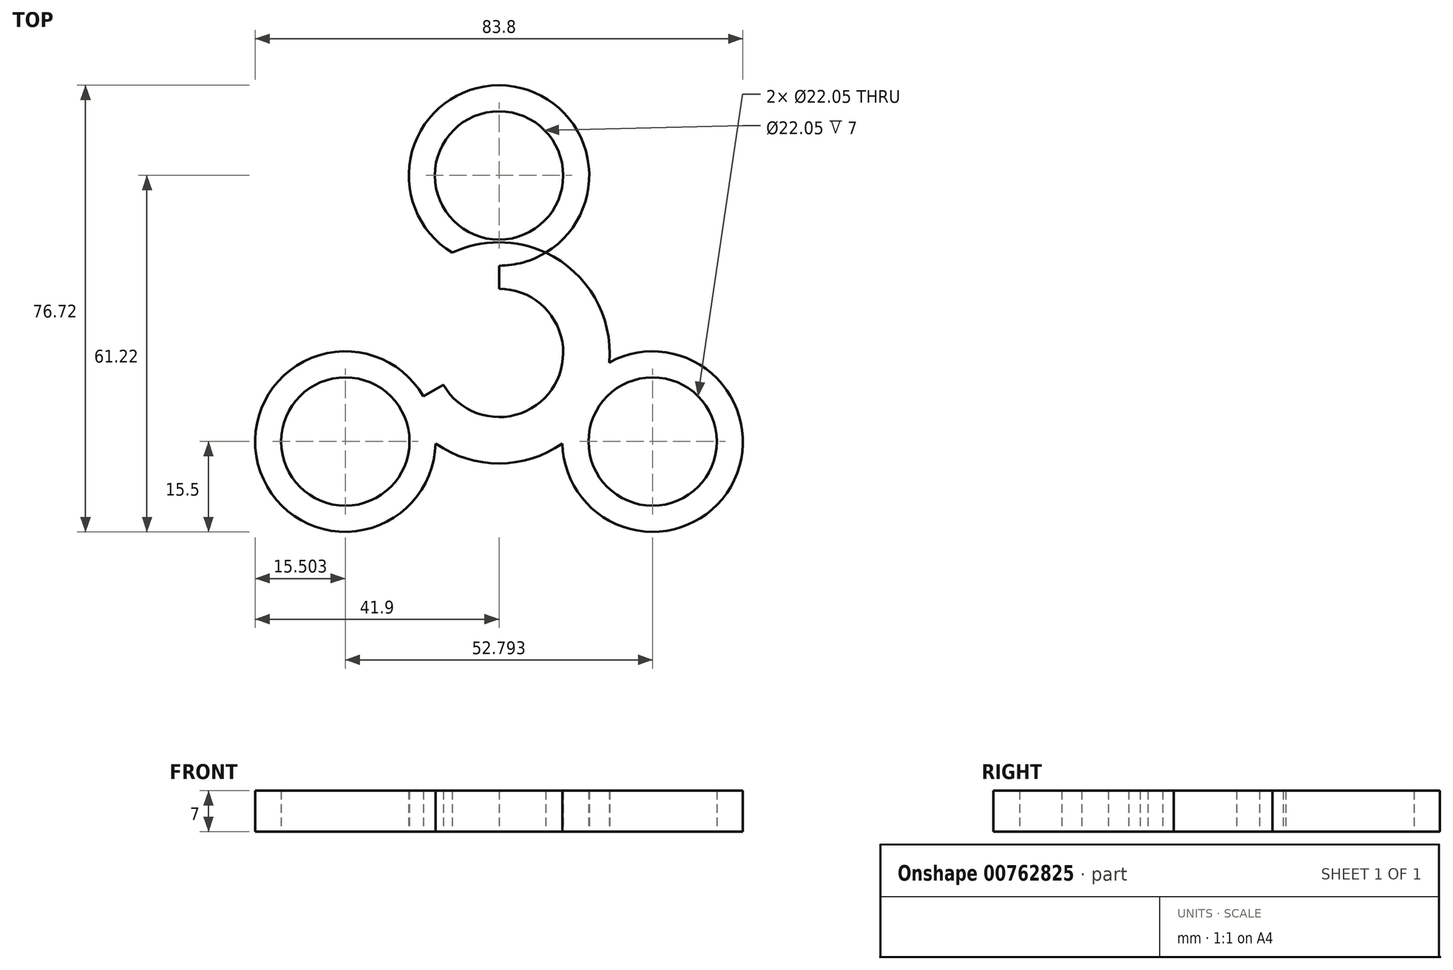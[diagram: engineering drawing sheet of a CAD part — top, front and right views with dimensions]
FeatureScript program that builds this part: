
annotation { "Feature Type Name" : "Feature", "Feature Type Description" : "" }
export const myFeature = defineFeature(function(context is Context, id is Id, definition is map)
    precondition{}
    {
        {
            var Q0;
            Q0=qCreatedBy(makeId("Top.planeOp"),FACE);
            var sketch = newSketch(context, id + "F0", { "sketchPlane" : qUnion([Q0])});
            skCircle(sketch, "E0", {"center": v(0, 0) * mm, "radius": 11.03 * mm});
            skLineSegment(sketch, "E1", {"start": v(0, 0) * mm, "end": v(0, 30.48) * mm});
            skLineSegment(sketch, "E2", {"start": v(0, 30.48) * mm, "end": v(0, 0) * mm});
            skLineSegment(sketch, "E3", {"start": v(0, 0) * mm, "end": v(26.4, -15.24) * mm});
            skLineSegment(sketch, "E4", {"start": v(0, 0) * mm, "end": v(-26.4, -15.24) * mm});
            skCircle(sketch, "E5", {"center": v(0, 30.48) * mm, "radius": 11.03 * mm});
            skCircle(sketch, "E6", {"center": v(26.4, -15.24) * mm, "radius": 11.03 * mm});
            skCircle(sketch, "E7", {"center": v(-26.4, -15.24) * mm, "radius": 11.03 * mm});
            skCircle(sketch, "E8", {"center": v(0, 30.48) * mm, "radius": 15.5 * mm});
            skCircle(sketch, "E9", {"center": v(26.4, -15.24) * mm, "radius": 15.5 * mm});
            skCircle(sketch, "E10", {"center": v(-26.4, -15.24) * mm, "radius": 15.5 * mm});
            skCircle(sketch, "E11", {"center": v(0, 0) * mm, "radius": 19 * mm});
            skLineSegment(sketch, "E12", {"start": v(18.98, 0.97) * mm, "end": v(8.47, 7.06) * mm});
            skSolve(sketch);
        }
        {
            var Q0;
            Q0=makeQuery(id+"F0.imprint","IMPRINT",FACE,{"disambiguationData":[TD([[makeQuery(id+"F0.imprint","IMPRINT",EDGE,{"derivedFrom":sQuery(id+"F0.wireOp",EDGE,"E5")}),-1.0]])]});
            var Q1;
            {var subQ0=sQuery(id+"F0.wireOp",EDGE,"E2");var subQ1=sQuery(id+"F0.wireOp",EDGE,"E0");var subQ2=makeQuery(id+"F0.imprint","INTERSECT",VERTEX,{"derivedFrom":[subQ1,subQ0]});Q1=makeQuery(id+"F0.imprint","IMPRINT",FACE,{"disambiguationData":[TD([[makeQuery(id+"F0.imprint","IMPRINT",EDGE,{"disambiguationData":[TD([[subQ2,-1.0]])],"derivedFrom":subQ1}),-1.0]])]});}
            var Q2;
            {var subQ5=sQuery(id+"F0.wireOp",EDGE,"E12");Q2=makeQuery(id+"F0.imprint","IMPRINT",FACE,{"disambiguationData":[TD([[makeQuery(id+"F0.imprint","IMPRINT",EDGE,{"derivedFrom":subQ5}),-1.0]])]});}
            var Q3;
            {var subQ0=sQuery(id+"F0.wireOp",EDGE,"E11");var subQ1=sQuery(id+"F0.wireOp",EDGE,"E2");var subQ2=makeQuery(id+"F0.imprint","INTERSECT",VERTEX,{"derivedFrom":[subQ1,subQ0]});Q3=makeQuery(id+"F0.imprint","IMPRINT",FACE,{"disambiguationData":[TD([[makeQuery(id+"F0.imprint","IMPRINT",EDGE,{"disambiguationData":[TD([[subQ2,-1.0]])],"derivedFrom":subQ1}),1.0]])]});}
            var Q4;
            {var subQ0=sQuery(id+"F0.wireOp",EDGE,"E11");var subQ1=sQuery(id+"F0.wireOp",EDGE,"E2");var subQ2=makeQuery(id+"F0.imprint","INTERSECT",VERTEX,{"derivedFrom":[subQ1,subQ0]});Q4=makeQuery(id+"F0.imprint","IMPRINT",FACE,{"disambiguationData":[TD([[makeQuery(id+"F0.imprint","IMPRINT",EDGE,{"disambiguationData":[TD([[subQ2,-1.0]])],"derivedFrom":subQ1}),-1.0]])]});}
            var Q5;
            Q5=makeQuery(id+"F0.imprint","IMPRINT",FACE,{"disambiguationData":[TD([[makeQuery(id+"F0.imprint","IMPRINT",EDGE,{"derivedFrom":sQuery(id+"F0.wireOp",EDGE,"E7")}),-1.0]])]});
            var Q6;
            {var subQ0=sQuery(id+"F0.wireOp",EDGE,"E11");var subQ1=sQuery(id+"F0.wireOp",EDGE,"E4");var subQ2=makeQuery(id+"F0.imprint","INTERSECT",VERTEX,{"derivedFrom":[subQ1,subQ0]});Q6=makeQuery(id+"F0.imprint","IMPRINT",FACE,{"disambiguationData":[TD([[makeQuery(id+"F0.imprint","IMPRINT",EDGE,{"disambiguationData":[TD([[subQ2,1.0]])],"derivedFrom":subQ1}),-1.0]])]});}
            var Q7;
            {var subQ0=sQuery(id+"F0.wireOp",EDGE,"E11");var subQ1=sQuery(id+"F0.wireOp",EDGE,"E4");var subQ2=makeQuery(id+"F0.imprint","INTERSECT",VERTEX,{"derivedFrom":[subQ1,subQ0]});Q7=makeQuery(id+"F0.imprint","IMPRINT",FACE,{"disambiguationData":[TD([[makeQuery(id+"F0.imprint","IMPRINT",EDGE,{"disambiguationData":[TD([[subQ2,1.0]])],"derivedFrom":subQ1}),1.0]])]});}
            var Q8;
            {var subQ7=sQuery(id+"F0.wireOp",EDGE,"E4");var subQ8=sQuery(id+"F0.wireOp",EDGE,"E0");var subQ9=makeQuery(id+"F0.imprint","INTERSECT",VERTEX,{"derivedFrom":[subQ8,subQ7]});Q8=makeQuery(id+"F0.imprint","IMPRINT",FACE,{"disambiguationData":[TD([[makeQuery(id+"F0.imprint","IMPRINT",EDGE,{"disambiguationData":[TD([[subQ9,-1.0]])],"derivedFrom":subQ8}),-1.0]])]});}
            var Q9;
            {var subQ0=sQuery(id+"F0.wireOp",EDGE,"E11");var subQ1=sQuery(id+"F0.wireOp",EDGE,"E3");var subQ2=makeQuery(id+"F0.imprint","INTERSECT",VERTEX,{"derivedFrom":[subQ1,subQ0]});Q9=makeQuery(id+"F0.imprint","IMPRINT",FACE,{"disambiguationData":[TD([[makeQuery(id+"F0.imprint","IMPRINT",EDGE,{"disambiguationData":[TD([[subQ2,1.0]])],"derivedFrom":subQ1}),-1.0]])]});}
            var Q10;
            {var subQ0=sQuery(id+"F0.wireOp",EDGE,"E12");Q10=makeQuery(id+"F0.imprint","IMPRINT",FACE,{"disambiguationData":[TD([[makeQuery(id+"F0.imprint","IMPRINT",EDGE,{"derivedFrom":subQ0}),1.0]])]});}
            var Q11;
            {var subQ0=sQuery(id+"F0.wireOp",EDGE,"E11");var subQ1=sQuery(id+"F0.wireOp",EDGE,"E3");var subQ2=makeQuery(id+"F0.imprint","INTERSECT",VERTEX,{"derivedFrom":[subQ1,subQ0]});Q11=makeQuery(id+"F0.imprint","IMPRINT",FACE,{"disambiguationData":[TD([[makeQuery(id+"F0.imprint","IMPRINT",EDGE,{"disambiguationData":[TD([[subQ2,1.0]])],"derivedFrom":subQ1}),1.0]])]});}
            var Q12;
            Q12=makeQuery(id+"F0.imprint","IMPRINT",FACE,{"disambiguationData":[TD([[makeQuery(id+"F0.imprint","IMPRINT",EDGE,{"derivedFrom":sQuery(id+"F0.wireOp",EDGE,"E6")}),-1.0]])]});
            extrude(context, id + "F1", {"entities" : qUnion([Q0, Q1, Q2, Q3, Q4, Q5, Q6, Q7, Q8, Q9, Q10, Q11, Q12]), "depth" : 7 * mm, "offsetDistance" : 25.4 * mm});
        }
    });
